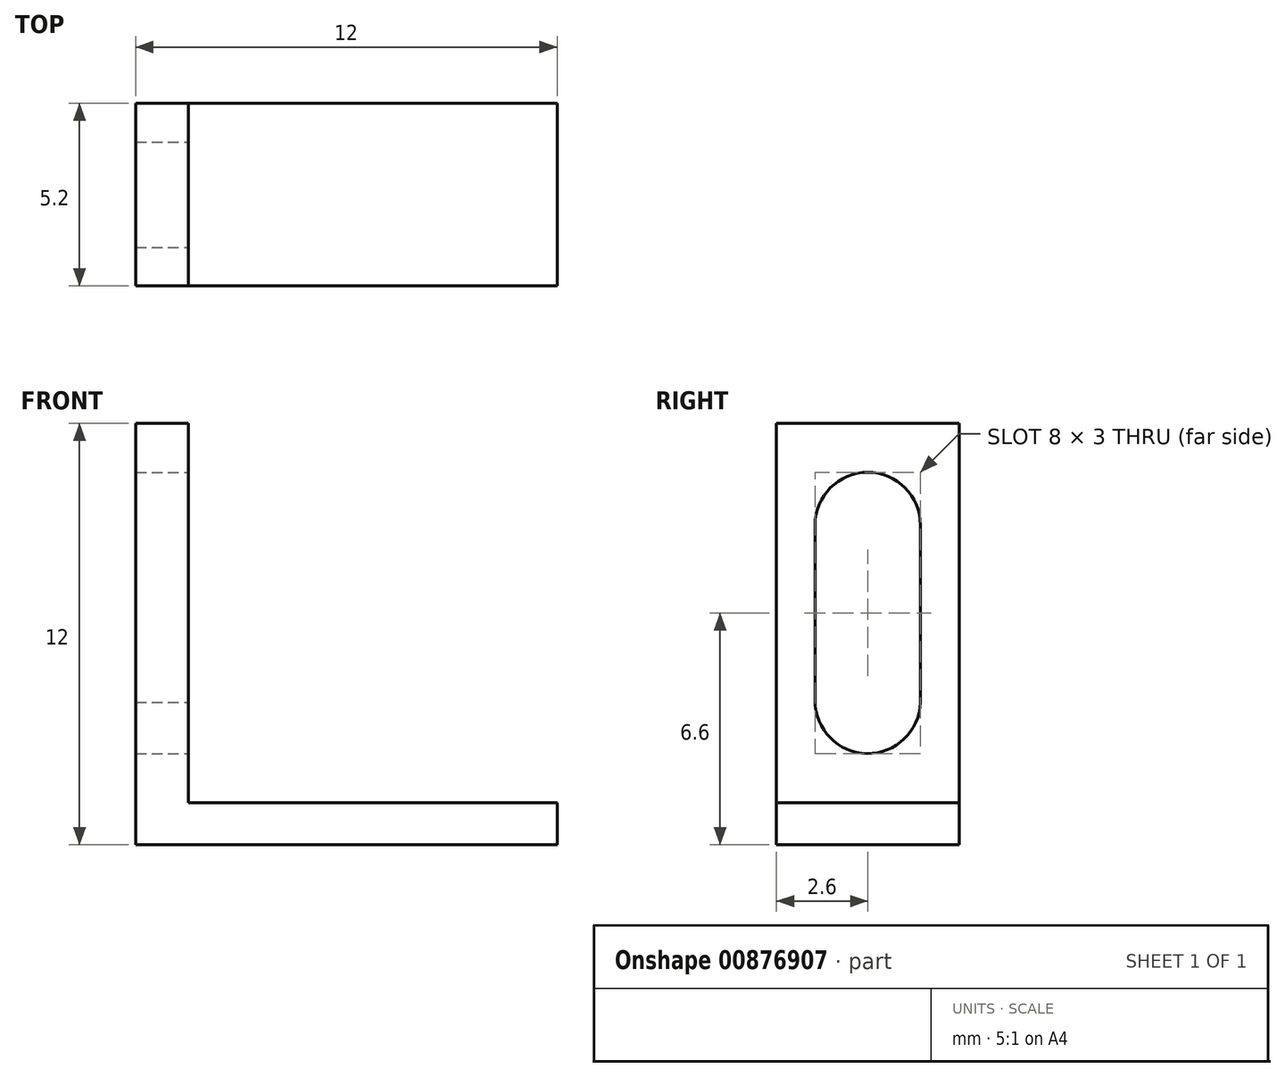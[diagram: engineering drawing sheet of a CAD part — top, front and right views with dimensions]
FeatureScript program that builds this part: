
annotation { "Feature Type Name" : "Feature", "Feature Type Description" : "" }
export const myFeature = defineFeature(function(context is Context, id is Id, definition is map)
    precondition{}
    {
        {
            var Q0;
            Q0=qCreatedBy(makeId("Front.planeOp"),FACE);
            var sketch = newSketch(context, id + "F0", { "sketchPlane" : qUnion([Q0])});
            skLineSegment(sketch, "E0", {"start": v(0, 0) * mm, "end": v(0, -12) * mm});
            skLineSegment(sketch, "E1", {"start": v(0, -12) * mm, "end": v(12, -12) * mm});
            skLineSegment(sketch, "E2", {"start": v(12, -12) * mm, "end": v(12, -10.8) * mm});
            skLineSegment(sketch, "E3", {"start": v(12, -10.8) * mm, "end": v(1.5, -10.8) * mm});
            skLineSegment(sketch, "E4", {"start": v(1.5, -10.8) * mm, "end": v(1.5, 0) * mm});
            skLineSegment(sketch, "E5", {"start": v(1.5, 0) * mm, "end": v(0, 0) * mm});
            skSolve(sketch);
        }
        {
            var Q0;
            Q0=makeQuery(id+"F0.imprint","IMPRINT",FACE,{"disambiguationData":[TD([[makeQuery(id+"F0.imprint","IMPRINT",EDGE,{"derivedFrom":sQuery(id+"F0.wireOp",EDGE,"E0")}),1.0]])]});
            extrude(context, id + "F1", {"entities" : qUnion([Q0]), "oppositeDirection" : true, "depth" : 5.2 * mm, "offsetDistance" : 25.4 * mm});
        }
        {
            var Q0;
            Q0=makeQuery(id+"F1.opExtrude","SWEPT_FACE",FACE,{"disambiguationData":[OSD([sQuery(id+"F0.wireOp",EDGE,"E4")])]});
            var sketch = newSketch(context, id + "F2", { "sketchPlane" : qUnion([Q0])});
            skPoint(sketch, "E6", {"position": v(1.1, -2.9) * mm});
            skPoint(sketch, "E7", {"position": v(1.1, -7.9) * mm});
            skLineSegment(sketch, "E8", {"start": v(1.1, -7.9) * mm, "end": v(1.1, -2.9) * mm});
            skLineSegment(sketch, "E9.MirrorCS", {"start": v(4.1, -7.95) * mm, "end": v(4.1, -2.9) * mm});
            skArc(sketch, "E10", {"start": v(4.1, -2.9) * mm, "mid": v(2.6, -1.4) * mm, "end": v(1.1, -2.9) * mm});
            skArc(sketch, "E11", {"start": v(1.1, -7.9) * mm, "mid": v(2.58, -9.4) * mm, "end": v(4.1, -7.95) * mm});
            skSolve(sketch);
        }
        {
            var Q0;
            Q0=makeQuery(id+"F2.imprint","IMPRINT",FACE,{"disambiguationData":[TD([[makeQuery(id+"F2.imprint","IMPRINT",EDGE,{"derivedFrom":sQuery(id+"F2.wireOp",EDGE,"E8")}),-1.0]])]});
            extrude(context, id + "F3", {"entities" : qUnion([Q0]), "operationType" : NewBodyOperationType.REMOVE, "oppositeDirection" : true, "depth" : 25.4 * mm, "offsetDistance" : 25.4 * mm});
        }
    });
